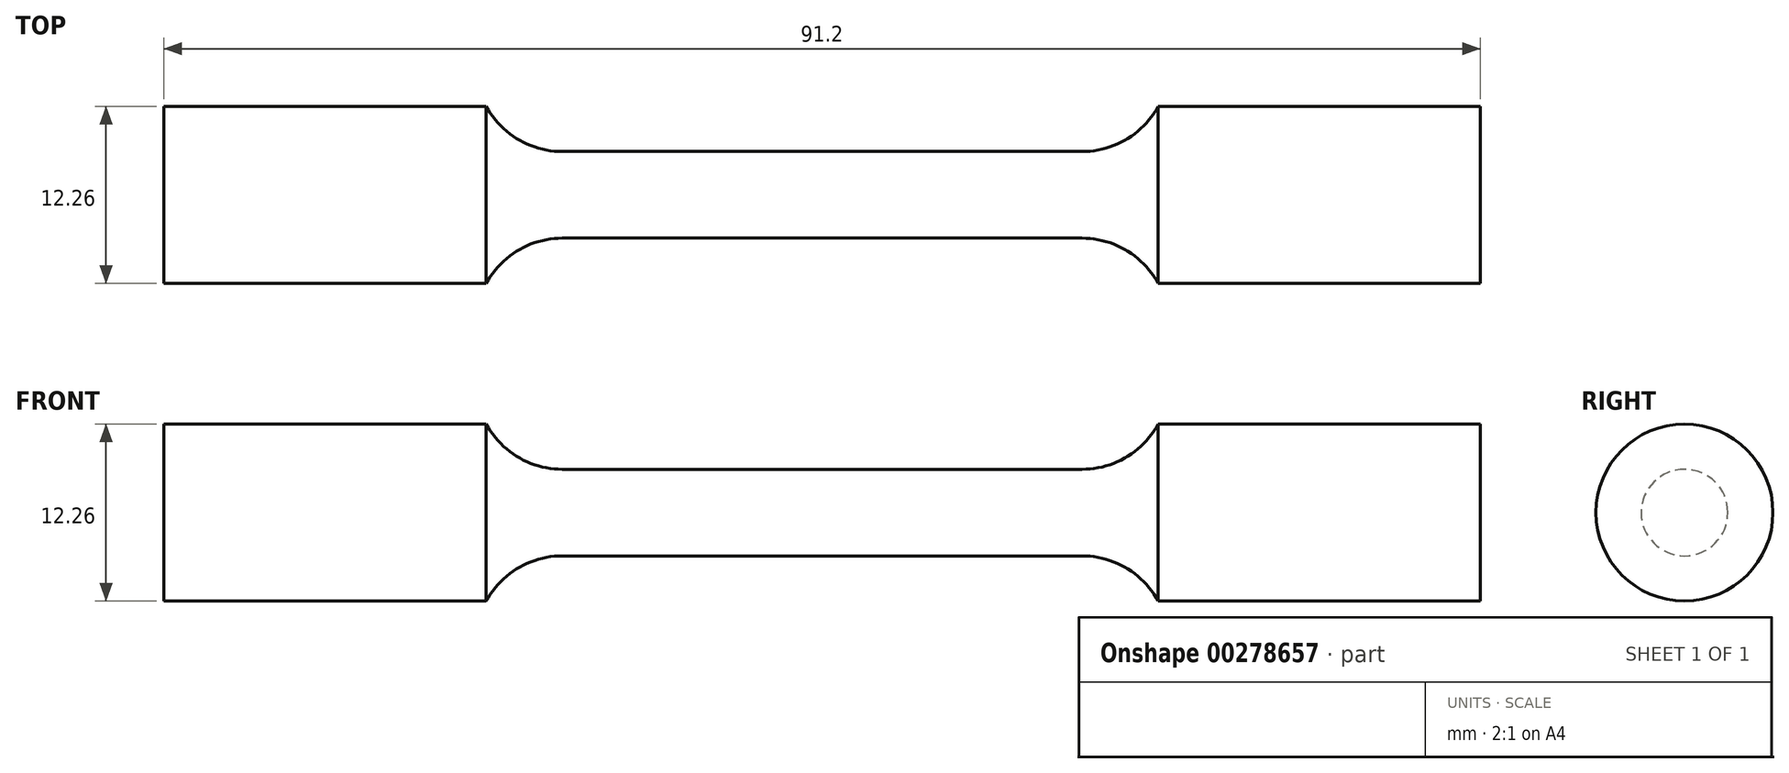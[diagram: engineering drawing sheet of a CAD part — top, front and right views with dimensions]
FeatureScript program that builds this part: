
annotation { "Feature Type Name" : "Feature", "Feature Type Description" : "" }
export const myFeature = defineFeature(function(context is Context, id is Id, definition is map)
    precondition{}
    {
        {
            var Q0;
            Q0=qCreatedBy(makeId("Front.planeOp"),FACE);
            var sketch = newSketch(context, id + "F0", { "sketchPlane" : qUnion([Q0])});
            skLineSegment(sketch, "E0", {"start": v(0, 3) * mm, "end": v(18, 3) * mm});
            skArc(sketch, "E1", {"start": v(18, 3) * mm, "mid": v(21.06, 3.84) * mm, "end": v(23.27, 6.13) * mm});
            skLineSegment(sketch, "E2", {"start": v(23.27, 6.13) * mm, "end": v(45.6, 6.13) * mm});
            skLineSegment(sketch, "E3", {"start": v(45.6, 6.13) * mm, "end": v(45.6, 0) * mm});
            skLineSegment(sketch, "E4.MirrorCS", {"start": v(0, 3) * mm, "end": v(-18, 3) * mm});
            skLineSegment(sketch, "E5.MirrorCS", {"start": v(-45.6, 6.13) * mm, "end": v(-45.6, 0) * mm});
            skLineSegment(sketch, "E6.MirrorCS", {"start": v(-23.27, 6.13) * mm, "end": v(-45.6, 6.13) * mm});
            skArc(sketch, "E7.MirrorCS", {"start": v(-18, 3) * mm, "mid": v(-21.06, 3.84) * mm, "end": v(-23.27, 6.13) * mm});
            skLineSegment(sketch, "E8", {"start": v(-45.6, 0) * mm, "end": v(45.6, 0) * mm});
            skSolve(sketch);
        }
        {
            var Q0;
            Q0 = qSketchRegion(id + "F0", true);
            var Q1;
            Q1=sQuery(id+"F0.wireOp",EDGE,"E8");
            revolve(context, id + "F1", {"entities" : qUnion([Q0]), "axis" : qUnion([Q1]), "revolveType" : RevolveType.FULL});
        }
    });
